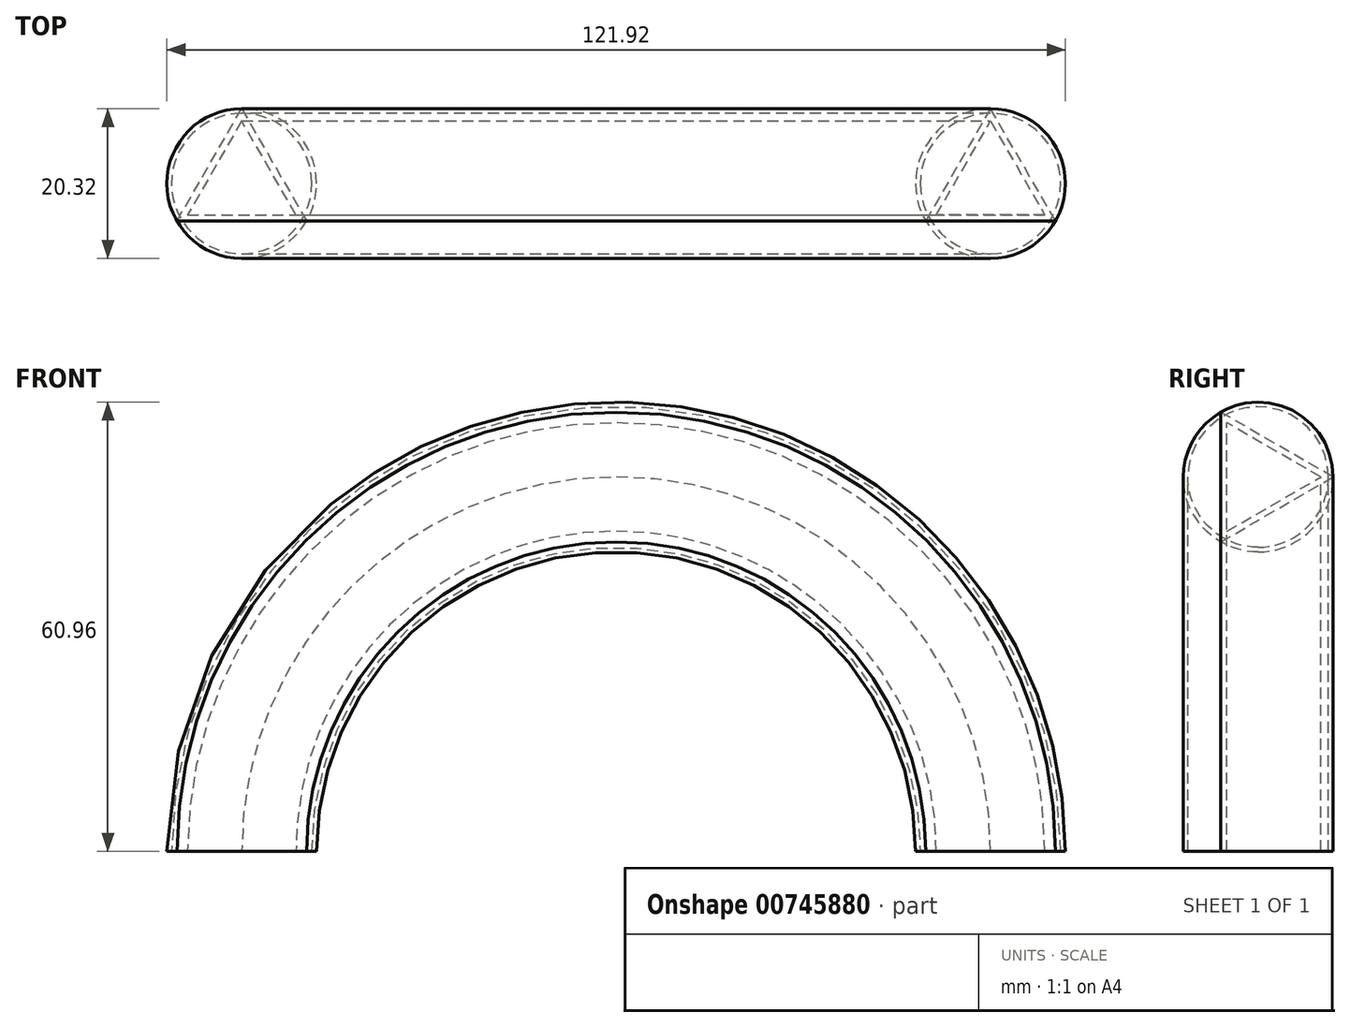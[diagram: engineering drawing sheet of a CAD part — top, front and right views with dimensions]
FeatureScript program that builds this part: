
annotation { "Feature Type Name" : "Feature", "Feature Type Description" : "" }
export const myFeature = defineFeature(function(context is Context, id is Id, definition is map)
    precondition{}
    {
        {
            var Q0;
            Q0=qCreatedBy(makeId("Front.planeOp"),FACE);
            var sketch = newSketch(context, id + "F0", { "sketchPlane" : qUnion([Q0])});
            skArc(sketch, "E0", {"start": v(50.8, 0) * mm, "mid": v(0, 50.8) * mm, "end": v(-50.8, 0) * mm});
            skSolve(sketch);
        }
        {
            var Q0;
            Q0=qCreatedBy(makeId("Top.planeOp"),FACE);
            var sketch = newSketch(context, id + "F1", { "sketchPlane" : qUnion([Q0])});
            skCircle(sketch, "E1", {"center": v(-50.8, 0) * mm, "radius": 9.53 * mm});
            skCircle(sketch, "E2", {"center": v(-50.8, 0) * mm, "radius": 10.16 * mm});
            skCircle(sketch, "E3", {"center": v(-50.8, 0) * mm, "radius": 8.5 * mm, "construction": true});
            skPoint(sketch, "E4", {"position": v(-50.8, -8.5) * mm});
            skPoint(sketch, "E5.trimOffspring.end.orphan", {"position": v(-50.8, -9.53) * mm});
            skSolve(sketch);
        }
        {
            var Q0;
            Q0=makeQuery(id+"F1.imprint","IMPRINT",FACE,{"disambiguationData":[TD([[makeQuery(id+"F1.imprint","IMPRINT",EDGE,{"derivedFrom":sQuery(id+"F1.wireOp",EDGE,"E1")}),-1.0]])]});
            var sketch = newSketch(context, id + "F2", { "sketchPlane" : qUnion([Q0])});
            skLineSegment(sketch, "E6", {"start": v(-50.8, 10.16) * mm, "end": v(-42, -5.08) * mm});
            skLineSegment(sketch, "E7", {"start": v(-42, -5.08) * mm, "end": v(-59.6, -5.08) * mm});
            skLineSegment(sketch, "E8", {"start": v(-59.6, -5.08) * mm, "end": v(-50.8, 10.16) * mm});
            skPoint(sketch, "E9", {"position": v(-50.8, -10.16) * mm});
            skLineSegment(sketch, "E10", {"start": v(-58.15, -4.25) * mm, "end": v(-43.45, -4.25) * mm});
            skLineSegment(sketch, "E11", {"start": v(-43.45, -4.25) * mm, "end": v(-50.8, 8.5) * mm});
            skLineSegment(sketch, "E12", {"start": v(-50.8, 8.5) * mm, "end": v(-58.15, -4.25) * mm});
            skSolve(sketch);
        }
        {
            var Q0;
            Q0 = qSketchRegion(id + "F1", true);
            var Q1;
            Q1 = qSketchRegion(id + "F2", true);
            var Q2;
            Q2 = qConstructionFilter(qBodyType(qCreatedBy(id + "F0" ,EDGE), BodyType.WIRE), ConstructionObject.NO);
            sweep(context, id + "F3", {"profiles" : qUnion([Q0, Q1]), "path" : qUnion([Q2])});
        }
    });
